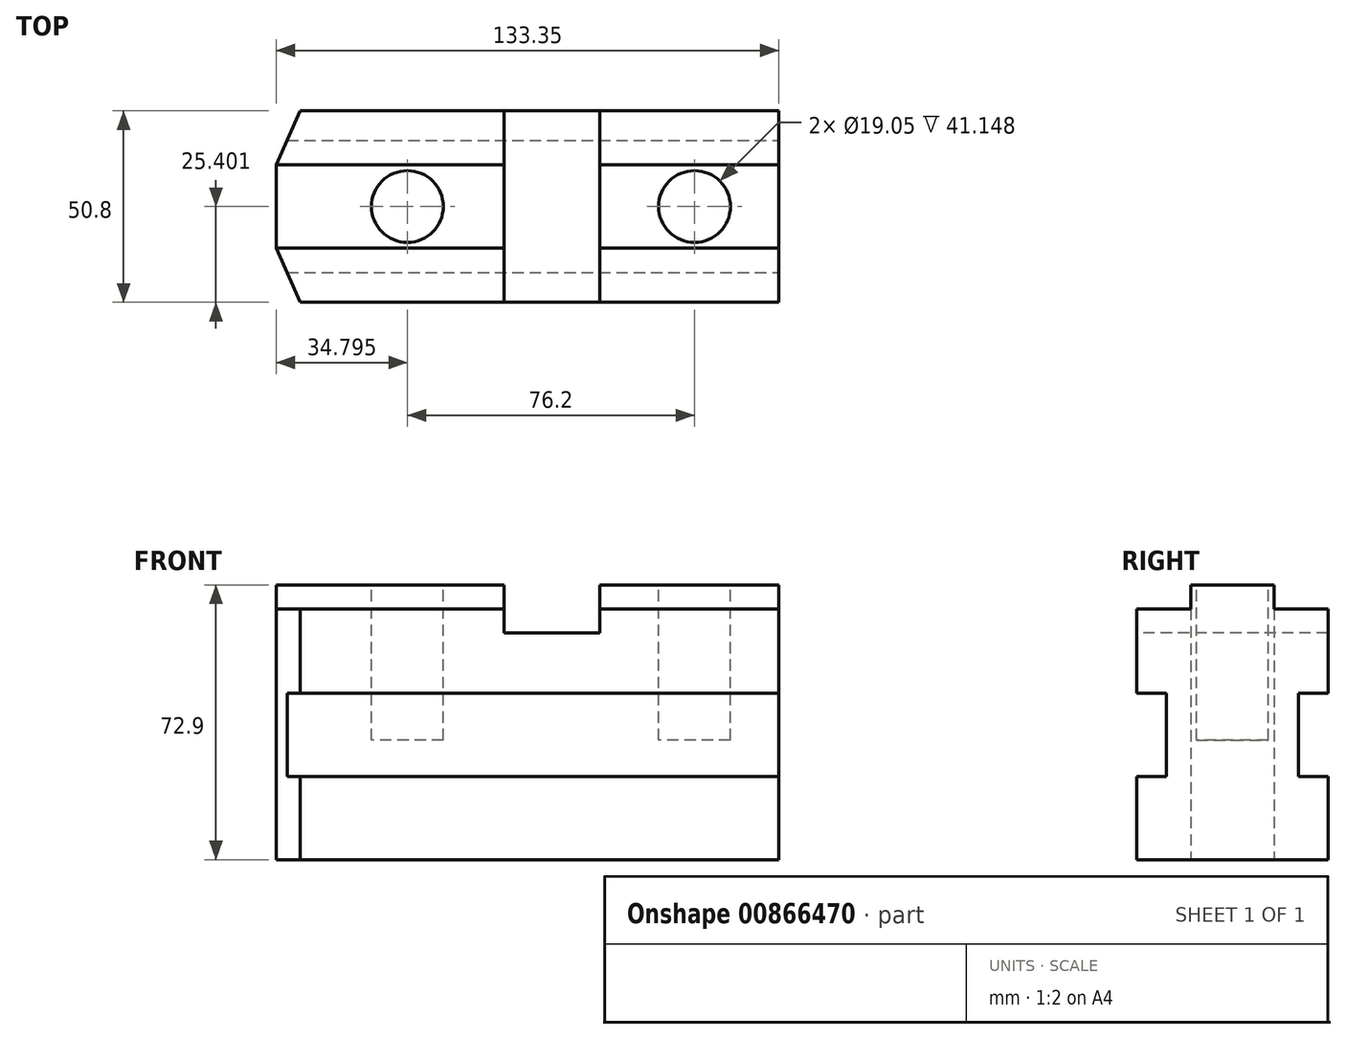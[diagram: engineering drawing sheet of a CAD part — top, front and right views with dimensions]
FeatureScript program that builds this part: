
annotation { "Feature Type Name" : "Feature", "Feature Type Description" : "" }
export const myFeature = defineFeature(function(context is Context, id is Id, definition is map)
    precondition{}
    {
        {
            var Q0;
            Q0=qCreatedBy(makeId("Top.planeOp"),FACE);
            var sketch = newSketch(context, id + "F0", { "sketchPlane" : qUnion([Q0])});
            skLineSegment(sketch, "E0", {"start": v(-84.21, 47.1) * mm, "end": v(42.79, 47.1) * mm});
            skLineSegment(sketch, "E1", {"start": v(42.79, 47.1) * mm, "end": v(42.79, -3.7) * mm});
            skLineSegment(sketch, "E2", {"start": v(42.79, -3.7) * mm, "end": v(-84.21, -3.7) * mm});
            skLineSegment(sketch, "E3", {"start": v(-84.21, -3.7) * mm, "end": v(-90.56, 10.65) * mm});
            skLineSegment(sketch, "E4", {"start": v(-90.56, 10.65) * mm, "end": v(-90.56, 32.75) * mm});
            skLineSegment(sketch, "E5", {"start": v(-90.56, 32.75) * mm, "end": v(-84.21, 47.1) * mm});
            skLineSegment(sketch, "E6", {"start": v(-90.56, 10.65) * mm, "end": v(42.79, 10.65) * mm});
            skLineSegment(sketch, "E7", {"start": v(-90.56, 32.75) * mm, "end": v(42.79, 32.75) * mm});
            skSolve(sketch);
        }
        {
            var Q0;
            Q0=makeQuery(id+"F0.imprint","IMPRINT",FACE,{"disambiguationData":[TD([[makeQuery(id+"F0.imprint","IMPRINT",EDGE,{"derivedFrom":sQuery(id+"F0.wireOp",EDGE,"E4")}),-1.0]])]});
            extrude(context, id + "F1", {"entities" : qUnion([Q0]), "depth" : 72.9 * mm, "offsetDistance" : 25.4 * mm});
        }
        {
            var Q0;
            {var subQ0=sQuery(id+"F0.wireOp",EDGE,"E0");Q0=makeQuery(id+"F0.imprint","IMPRINT",FACE,{"disambiguationData":[TD([[makeQuery(id+"F0.imprint","IMPRINT",EDGE,{"derivedFrom":subQ0}),-1.0]])]});}
            var Q1;
            {var subQ0=sQuery(id+"F0.wireOp",EDGE,"E2");Q1=makeQuery(id+"F0.imprint","IMPRINT",FACE,{"disambiguationData":[TD([[makeQuery(id+"F0.imprint","IMPRINT",EDGE,{"derivedFrom":subQ0}),-1.0]])]});}
            extrude(context, id + "F2", {"entities" : qUnion([Q0, Q1]), "operationType" : NewBodyOperationType.ADD, "depth" : 66.55 * mm, "offsetDistance" : 25.4 * mm});
        }
        {
            var Q0;
            Q0=makeQuery(id+"F1.opExtrude","CAP_EDGE",EDGE,{"disambiguationData":[OSD([sQuery(id+"F0.wireOp",EDGE,"E1")])],"isStart":false});
            cPoint(context, id + "F3", {"entities" : qUnion([Q0]), "parameter" : 0.5});
        }
        {
            var Q0;
            Q0 = qCreatedBy(id + "F3" ,VERTEX);
            var Q1;
            Q1=makeQuery(id+"F2.opExtrude","SWEPT_FACE",FACE,{"disambiguationData":[OSD([sQuery(id+"F0.wireOp",EDGE,"E2")])]});
            cPlane(context, id + "F4", {"entities" : qUnion([Q0, Q1]), "cplaneType" : CPlaneType.PLANE_POINT, "offset" : 25.4 * mm, "width" : 152.4 * mm, "height" : 152.4 * mm});
        }
        {
            var Q0;
            {var subQ0=sQuery(id+"F0.wireOp",EDGE,"E1");Q0=makeQuery(id+"F2.boolean.opBoolean","MERGE",FACE,{"derivedFrom":[makeQuery(id+"F1.opExtrude","SWEPT_FACE",FACE,{"disambiguationData":[OSD([subQ0])]}),makeQuery(id+"F2.opExtrude","SWEPT_FACE",FACE,{"disambiguationData":[OSD([subQ0]),TDD([makeQuery(id+"F0.imprint","IMPRINT",EDGE,{"disambiguationData":[TD([[makeQuery(id+"F0.imprint","INTERSECT",VERTEX,{"derivedFrom":[sQuery(id+"F0.wireOp",EDGE,"E0"),subQ0]}),-1.0]])],"derivedFrom":subQ0})])]}),makeQuery(id+"F2.opExtrude","SWEPT_FACE",FACE,{"disambiguationData":[OSD([subQ0]),TDD([makeQuery(id+"F0.imprint","IMPRINT",EDGE,{"disambiguationData":[TD([[makeQuery(id+"F0.imprint","INTERSECT",VERTEX,{"derivedFrom":[subQ0,sQuery(id+"F0.wireOp",EDGE,"E2")]}),1.0]])],"derivedFrom":subQ0})])]})]});}
            var sketch = newSketch(context, id + "F5", { "sketchPlane" : qUnion([Q0])});
            skLineSegment(sketch, "E8", {"start": v(-3.7, 22.1) * mm, "end": v(4.18, 22.1) * mm});
            skLineSegment(sketch, "E9", {"start": v(4.18, 22.1) * mm, "end": v(4.18, 44.2) * mm});
            skLineSegment(sketch, "E10", {"start": v(4.18, 44.2) * mm, "end": v(-3.7, 44.2) * mm});
            skSolve(sketch);
        }
        {
            var Q0;
            {var subQ0=sQuery(id+"F5.wireOp",EDGE,"E8");Q0=makeQuery(id+"F5.imprint","IMPRINT",FACE,{"disambiguationData":[TD([[makeQuery(id+"F5.imprint","IMPRINT",EDGE,{"derivedFrom":subQ0}),1.0]])]});}
            extrude(context, id + "F6", {"entities" : qUnion([Q0]), "operationType" : NewBodyOperationType.REMOVE, "endBound" : BoundingType.THROUGH_ALL, "oppositeDirection" : true, "depth" : 25.4 * mm, "offsetDistance" : 25.4 * mm});
        }
        {
            var Q0;
            Q0=makeQuery(id+"F1.opExtrude","SWEPT_BODY",BODY,{"disambiguationData":[OSD([sQuery(id+"F0.wireOp",EDGE,"E1"),sQuery(id+"F0.wireOp",EDGE,"E4"),sQuery(id+"F0.wireOp",EDGE,"E6"),sQuery(id+"F0.wireOp",EDGE,"E7")])]});
            var Q1;
            Q1=qCreatedBy(id+"F4.planeOp",FACE);
            mirror(context, id + "F7", {"operationType" : NewBodyOperationType.INTERSECT, "entities" : qUnion([Q0]), "mirrorPlane" : qUnion([Q1])});
        }
        {
            var Q0;
            {var subQ2=sQuery(id+"F0.wireOp",EDGE,"E2");Q0=makeQuery(id+"F6.boolean.opBoolean","SPLIT",FACE,{"disambiguationData":[TD([makeQuery(id+"F6.opExtrude","SWEPT_FACE",FACE,{"disambiguationData":[OSD([sQuery(id+"F5.wireOp",EDGE,"E10")])]})])],"derivedFrom":makeQuery(id+"F2.opExtrude","SWEPT_FACE",FACE,{"disambiguationData":[OSD([subQ2])]})});}
            var sketch = newSketch(context, id + "F8", { "sketchPlane" : qUnion([Q0])});
            skLineSegment(sketch, "E11", {"start": v(-30.11, 66.55) * mm, "end": v(-30.11, 60.2) * mm});
            skLineSegment(sketch, "E12", {"start": v(-30.11, 60.2) * mm, "end": v(-4.71, 60.2) * mm});
            skLineSegment(sketch, "E13", {"start": v(-4.71, 60.2) * mm, "end": v(-4.71, 66.55) * mm});
            skLineSegment(sketch, "E14", {"start": v(-30.11, 66.55) * mm, "end": v(-30.11, 81.92) * mm});
            skLineSegment(sketch, "E15", {"start": v(-30.11, 81.92) * mm, "end": v(-4.71, 81.92) * mm});
            skLineSegment(sketch, "E16", {"start": v(-4.71, 81.92) * mm, "end": v(-4.71, 66.55) * mm});
            skSolve(sketch);
        }
        {
            var Q0;
            {var subQ0=sQuery(id+"F8.wireOp",EDGE,"E14");Q0=makeQuery(id+"F8.imprint","IMPRINT",FACE,{"disambiguationData":[TD([[makeQuery(id+"F8.imprint","IMPRINT",EDGE,{"derivedFrom":subQ0}),-1.0]])]});}
            var Q1;
            {var subQ0=sQuery(id+"F8.wireOp",EDGE,"E11");Q1=makeQuery(id+"F8.imprint","IMPRINT",FACE,{"disambiguationData":[TD([[makeQuery(id+"F8.imprint","IMPRINT",EDGE,{"derivedFrom":subQ0}),1.0]])]});}
            extrude(context, id + "F9", {"entities" : qUnion([Q0, Q1]), "operationType" : NewBodyOperationType.REMOVE, "endBound" : BoundingType.THROUGH_ALL, "oppositeDirection" : true, "depth" : 25.4 * mm, "offsetDistance" : 25.4 * mm});
        }
        {
            var Q0;
            {var subQ0=sQuery(id+"F0.wireOp",EDGE,"E4");var subQ1=sQuery(id+"F0.wireOp",EDGE,"E6");var subQ2=sQuery(id+"F0.wireOp",EDGE,"E7");Q0=makeQuery(id+"F9.boolean.opBoolean","SPLIT",FACE,{"disambiguationData":[TD([makeQuery(id+"F1.opExtrude","SWEPT_FACE",FACE,{"disambiguationData":[OSD([subQ0])]})])],"derivedFrom":makeQuery(id+"F1.opExtrude","CAP_FACE",FACE,{"disambiguationData":[OSD([sQuery(id+"F0.wireOp",EDGE,"E1"),subQ0,subQ1,subQ2])],"isStart":false})});}
            var sketch = newSketch(context, id + "F10", { "sketchPlane" : qUnion([Q0])});
            skCircle(sketch, "E17", {"center": v(-55.76, 21.7) * mm, "radius": 9.53 * mm});
            skPoint(sketch, "E17.centerSnap0", {"position": v(-90.56, 21.7) * mm});
            skCircle(sketch, "E18", {"center": v(20.44, 21.7) * mm, "radius": 9.53 * mm});
            skPoint(sketch, "E18.centerSnap0", {"position": v(-30.11, 21.7) * mm});
            skSolve(sketch);
        }
        {
            var Q0;
            Q0 = qSketchRegion(id + "F10", true);
            extrude(context, id + "F11", {"entities" : qUnion([Q0]), "operationType" : NewBodyOperationType.REMOVE, "oppositeDirection" : true, "depth" : 41.15 * mm, "offsetDistance" : 25.4 * mm});
        }
    });
